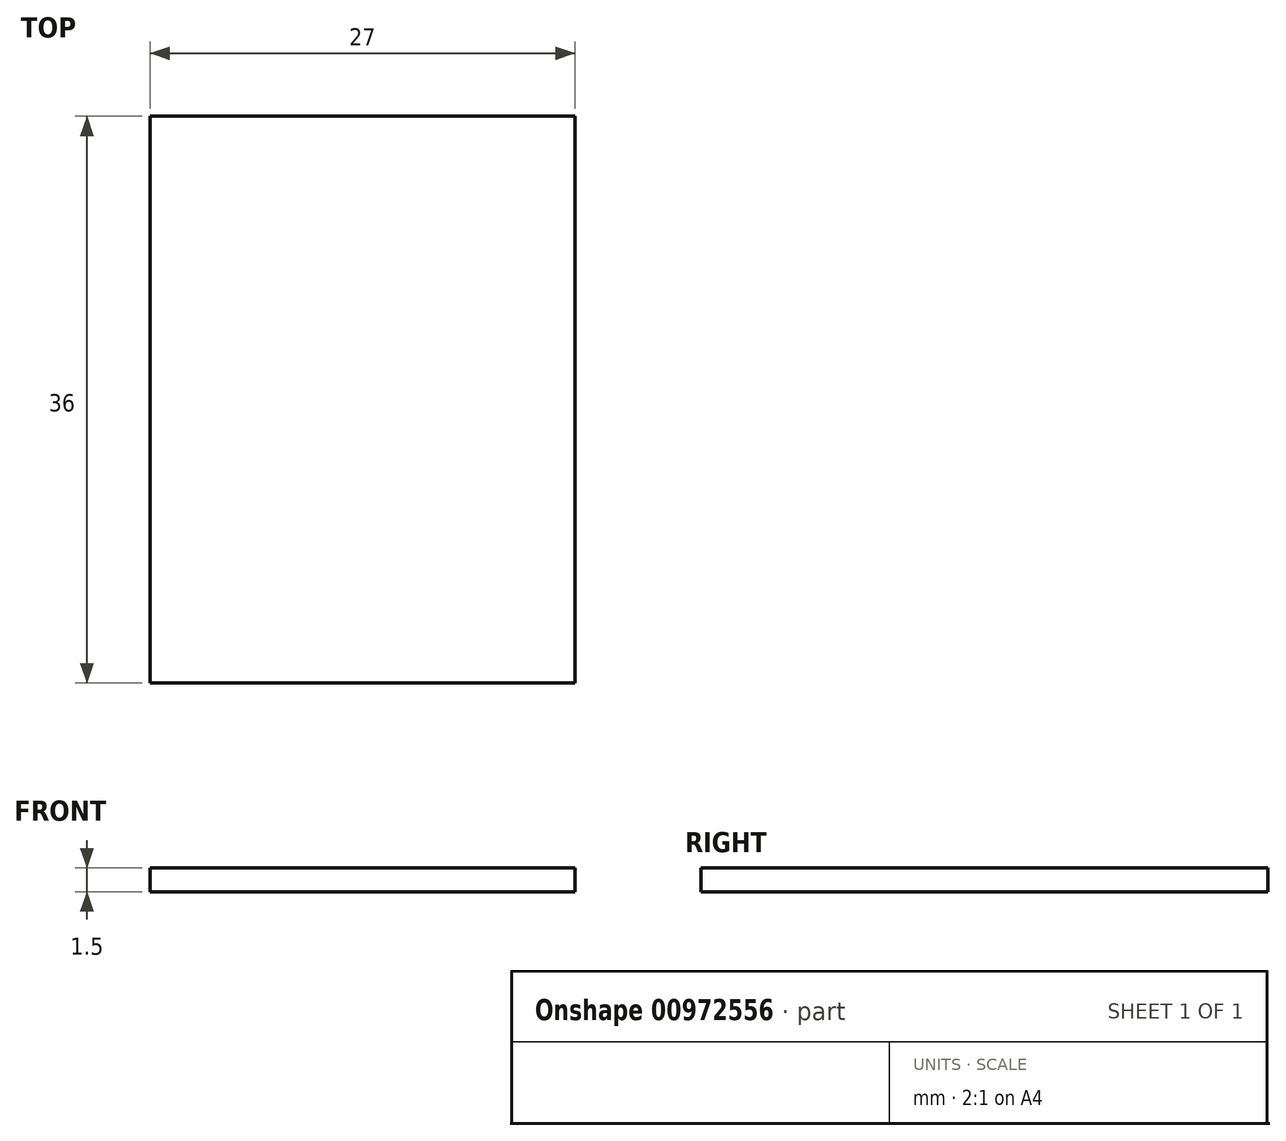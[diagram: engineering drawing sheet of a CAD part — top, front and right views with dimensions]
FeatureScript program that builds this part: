
annotation { "Feature Type Name" : "Feature", "Feature Type Description" : "" }
export const myFeature = defineFeature(function(context is Context, id is Id, definition is map)
    precondition{}
    {
        {
            var Q0;
            Q0=qCreatedBy(makeId("Top.planeOp"),FACE);
            var sketch = newSketch(context, id + "F0", { "sketchPlane" : qUnion([Q0])});
            skLineSegment(sketch, "E0.bottom", {"start": v(-13.5, 18) * mm, "end": v(13.5, 18) * mm});
            skLineSegment(sketch, "E0.top", {"start": v(-13.5, -18) * mm, "end": v(13.5, -18) * mm});
            skLineSegment(sketch, "E0.left", {"start": v(-13.5, 18) * mm, "end": v(-13.5, -18) * mm});
            skLineSegment(sketch, "E0.right", {"start": v(13.5, 18) * mm, "end": v(13.5, -18) * mm});
            skPoint(sketch, "E0.middle", {"position": v(0, 0) * mm});
            skLineSegment(sketch, "E1.0", {"start": v(-15, 19.5) * mm, "end": v(-15, -19.5) * mm});
            skLineSegment(sketch, "E1.1", {"start": v(-15, 19.5) * mm, "end": v(15, 19.5) * mm});
            skLineSegment(sketch, "E1.2", {"start": v(15, 19.5) * mm, "end": v(15, -19.5) * mm});
            skLineSegment(sketch, "E1.3", {"start": v(-15, -19.5) * mm, "end": v(15, -19.5) * mm});
            skSolve(sketch);
        }
        {
            var Q0;
            Q0=makeQuery(id+"F0.imprint","IMPRINT",FACE,{"disambiguationData":[TD([[makeQuery(id+"F0.imprint","IMPRINT",EDGE,{"derivedFrom":sQuery(id+"F0.wireOp",EDGE,"E0.bottom")}),-1.0]])]});
            extrude(context, id + "F1", {"entities" : qUnion([Q0]), "depth" : 1.5 * mm, "offsetDistance" : 25 * mm});
        }
    });
